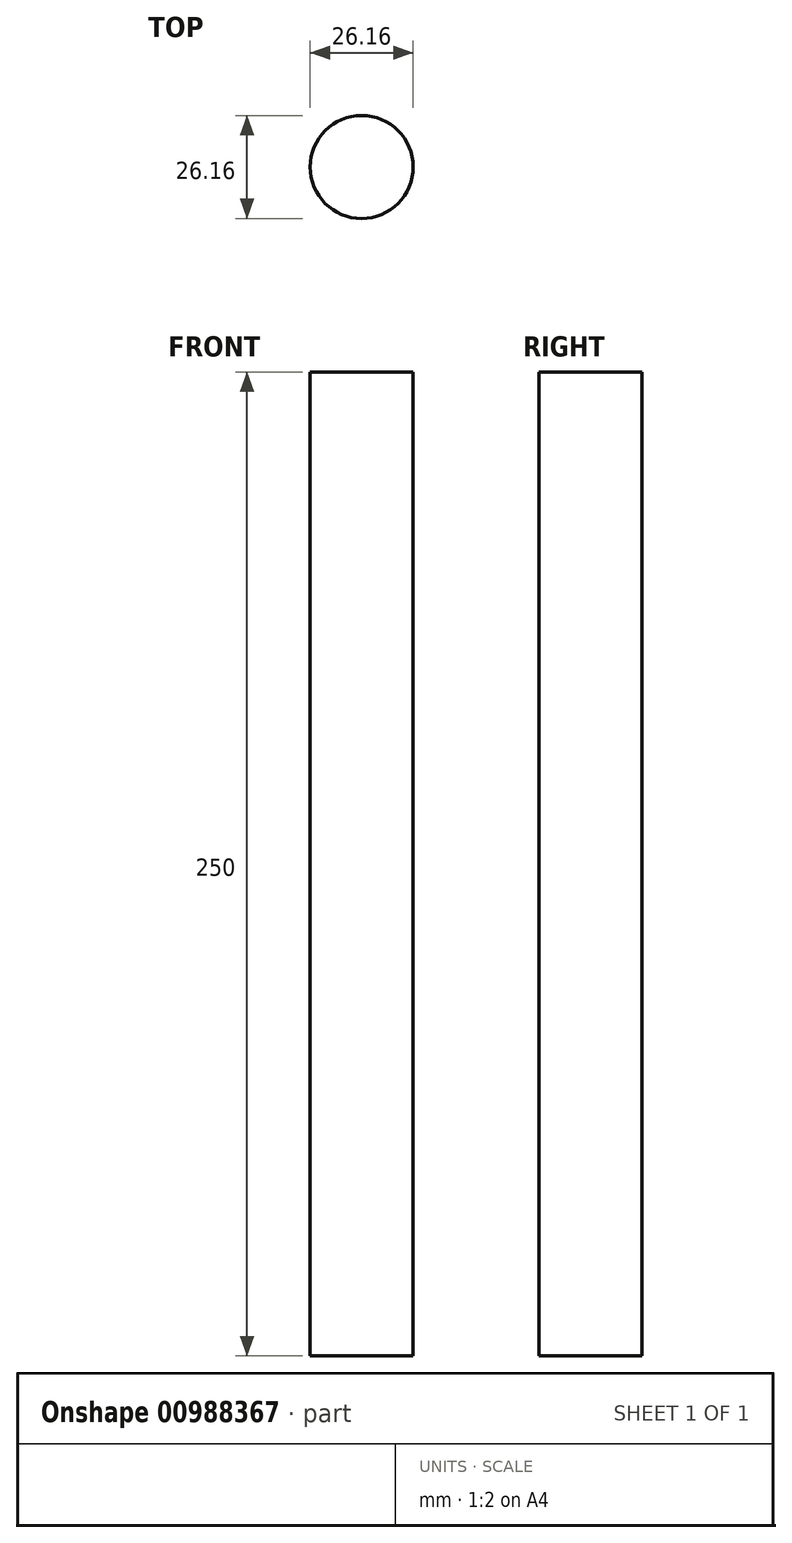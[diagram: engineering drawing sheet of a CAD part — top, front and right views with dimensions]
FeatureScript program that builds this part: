
annotation { "Feature Type Name" : "Feature", "Feature Type Description" : "" }
export const myFeature = defineFeature(function(context is Context, id is Id, definition is map)
    precondition{}
    {
        {
            var Q0;
            Q0=qCreatedBy(makeId("Top.planeOp"),FACE);
            var sketch = newSketch(context, id + "F0", { "sketchPlane" : qUnion([Q0])});
            skCircle(sketch, "E0", {"center": v(0, 0) * mm, "radius": 13.08 * mm});
            skSolve(sketch);
        }
        {
            var Q0;
            Q0=makeQuery(id+"F0.imprint","IMPRINT",FACE,{"disambiguationData":[TD([[makeQuery(id+"F0.imprint","IMPRINT",EDGE,{"derivedFrom":sQuery(id+"F0.wireOp",EDGE,"E0")}),1.0]])]});
            extrude(context, id + "F1", {"entities" : qUnion([Q0]), "oppositeDirection" : true, "depth" : 250 * mm, "offsetDistance" : 25 * mm});
        }
    });
